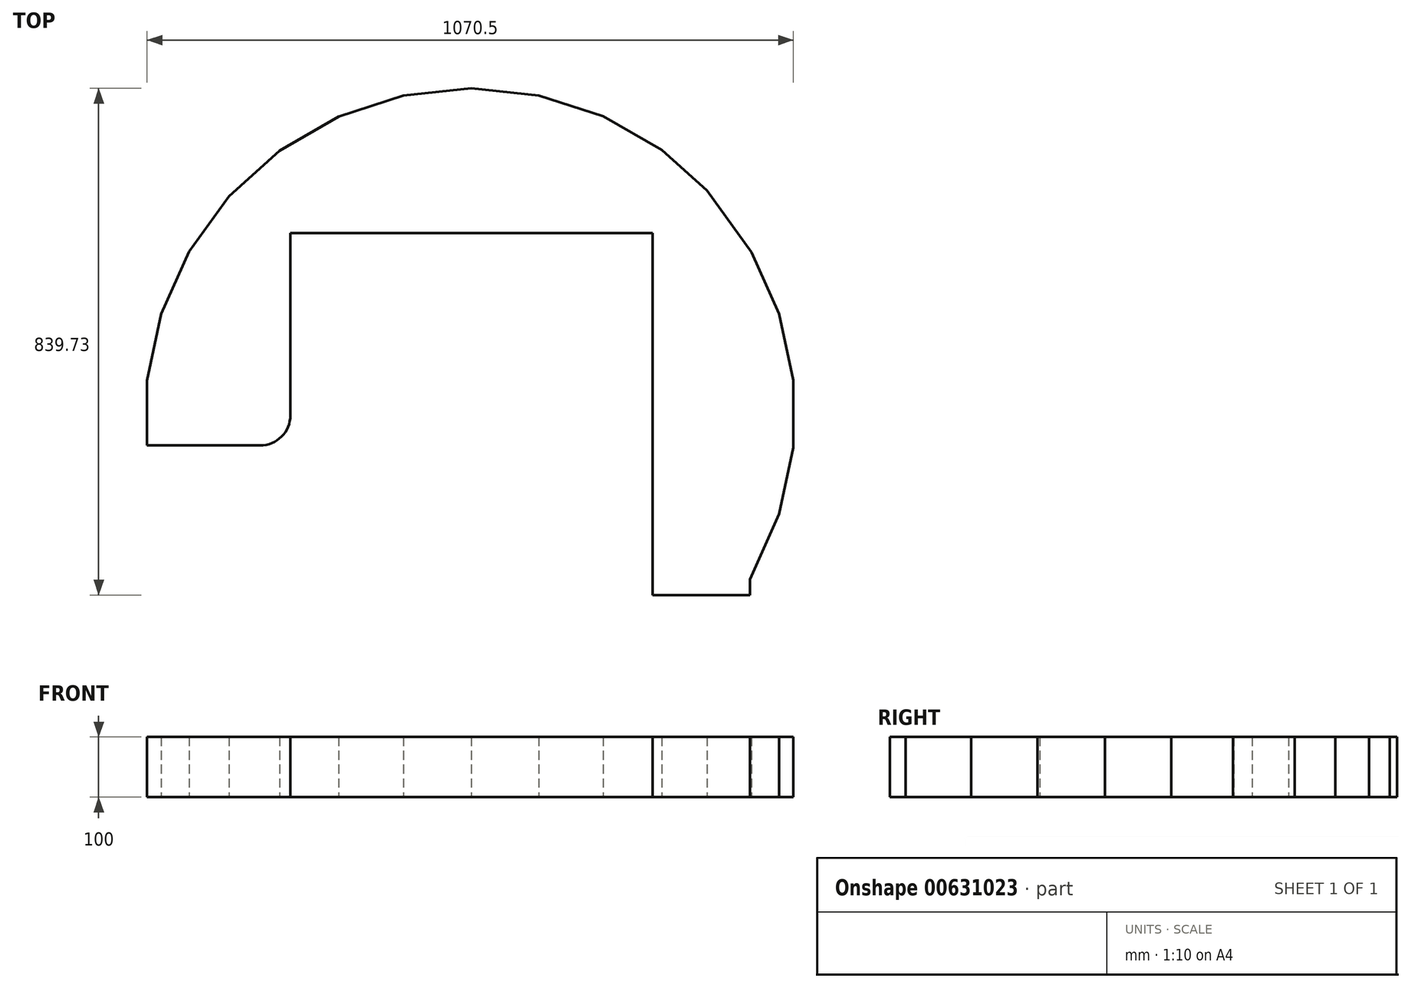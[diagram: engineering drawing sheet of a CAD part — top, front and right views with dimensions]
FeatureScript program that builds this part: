
annotation { "Feature Type Name" : "Feature", "Feature Type Description" : "" }
export const myFeature = defineFeature(function(context is Context, id is Id, definition is map)
    precondition{}
    {
        {
            var Q0;
            Q0=qCreatedBy(makeId("Top.planeOp"),FACE);
            var sketch = newSketch(context, id + "F0", { "sketchPlane" : qUnion([Q0])});
            skLineSegment(sketch, "E0.top", {"start": v(-250, 300) * mm, "end": v(250, 300) * mm});
            skLineSegment(sketch, "E0.left", {"start": v(-300, -2.1) * mm, "end": v(-300, 250) * mm});
            skLineSegment(sketch, "E0.right", {"start": v(300, -300) * mm, "end": v(300, 250) * mm});
            skPoint(sketch, "E0.middle", {"position": v(0, 0) * mm});
            skLineSegment(sketch, "E1", {"start": v(-537.3, -52.1) * mm, "end": v(-350, -52.1) * mm});
            skPoint(sketch, "E2.end.orphan", {"position": v(-300, -300) * mm});
            skLineSegment(sketch, "E3", {"start": v(300, -300) * mm, "end": v(461.55, -300) * mm});
            skPoint(sketch, "E4.visualSharp", {"position": v(-300, 300) * mm});
            skPoint(sketch, "E5.visualSharp", {"position": v(-300, -52.1) * mm});
            skPoint(sketch, "E6.visualSharp", {"position": v(300, 300) * mm});
            skLineSegment(sketch, "E7", {"start": v(-300, 250) * mm, "end": v(-300, 300) * mm});
            skLineSegment(sketch, "E8", {"start": v(-300, 300) * mm, "end": v(-250, 300) * mm});
            skLineSegment(sketch, "E9", {"start": v(250, 300) * mm, "end": v(300, 300) * mm});
            skLineSegment(sketch, "E10", {"start": v(300, 300) * mm, "end": v(300, 250) * mm});
            skLineSegment(sketch, "E11", {"start": v(-350, -52.1) * mm, "end": v(-350, -52.1) * mm});
            skLineSegment(sketch, "E12", {"start": v(-300, -2.1) * mm, "end": v(-300, -2.1) * mm});
            skLineSegment(sketch, "E13.0", {"start": v(509.88, -165.6) * mm, "end": v(461.55, -274.15) * mm});
            skLineSegment(sketch, "E13.1", {"start": v(533.2, -55.92) * mm, "end": v(509.88, -165.6) * mm});
            skLineSegment(sketch, "E13.2", {"start": v(533.16, 56.2) * mm, "end": v(533.2, -55.92) * mm});
            skLineSegment(sketch, "E13.3", {"start": v(509.8, 165.89) * mm, "end": v(533.16, 56.2) * mm});
            skLineSegment(sketch, "E13.4", {"start": v(464.16, 268.3) * mm, "end": v(509.8, 165.89) * mm});
            skLineSegment(sketch, "E13.5", {"start": v(390.06, 370.18) * mm, "end": v(464.16, 268.3) * mm});
            skLineSegment(sketch, "E13.6", {"start": v(315.2, 437.5) * mm, "end": v(390.06, 370.18) * mm});
            skLineSegment(sketch, "E13.7", {"start": v(218.04, 493.5) * mm, "end": v(315.2, 437.5) * mm});
            skLineSegment(sketch, "E13.8", {"start": v(-467.85, 269.18) * mm, "end": v(-401.6, 360.63) * mm});
            skLineSegment(sketch, "E13.9", {"start": v(-513.78, 166.02) * mm, "end": v(-467.85, 269.18) * mm});
            skLineSegment(sketch, "E13.10", {"start": v(-537.3, 55.32) * mm, "end": v(-513.78, 166.02) * mm});
            skLineSegment(sketch, "E13.12", {"start": v(-401.6, 360.63) * mm, "end": v(-317.8, 436.27) * mm});
            skLineSegment(sketch, "E13.13", {"start": v(-317.8, 436.27) * mm, "end": v(-220.1, 492.82) * mm});
            skLineSegment(sketch, "E13.14", {"start": v(-220.1, 492.82) * mm, "end": v(-112.79, 527.82) * mm});
            skLineSegment(sketch, "E13.15", {"start": v(-112.79, 527.82) * mm, "end": v(-0.53, 539.73) * mm});
            skLineSegment(sketch, "E13.16", {"start": v(-0.53, 539.73) * mm, "end": v(111.37, 528.07) * mm});
            skLineSegment(sketch, "E13.17", {"start": v(111.37, 528.07) * mm, "end": v(218.04, 493.5) * mm});
            skLineSegment(sketch, "E14", {"start": v(-537.3, 55.32) * mm, "end": v(-537.3, -52.1) * mm});
            skLineSegment(sketch, "E15", {"start": v(461.55, -274.15) * mm, "end": v(461.55, -300) * mm});
            skArc(sketch, "E16.filletArc", {"start": v(-350, -52.1) * mm, "mid": v(-314.64, -37.45) * mm, "end": v(-300, -2.1) * mm});
            skSolve(sketch);
        }
        {
            var Q0;
            Q0 = qSketchRegion(id + "F0", true);
            extrude(context, id + "F1", {"entities" : qUnion([Q0]), "depth" : 100 * mm, "offsetDistance" : 25 * mm});
        }
    });
